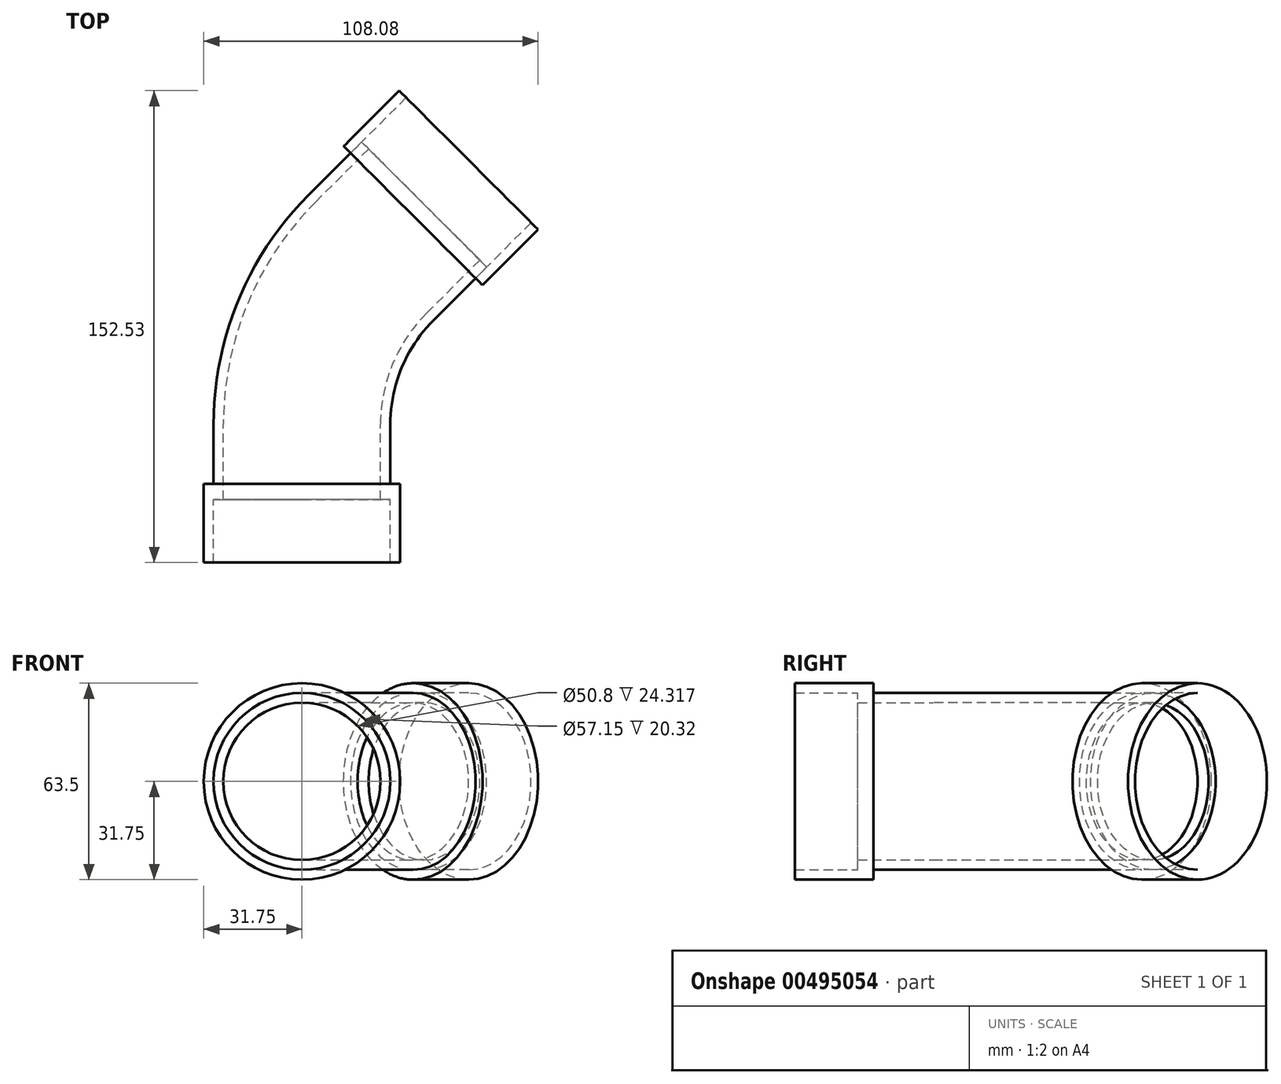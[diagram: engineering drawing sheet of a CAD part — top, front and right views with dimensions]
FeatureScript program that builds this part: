
annotation { "Feature Type Name" : "Feature", "Feature Type Description" : "" }
export const myFeature = defineFeature(function(context is Context, id is Id, definition is map)
    precondition{}
    {
        {
            var Q0;
            Q0=qCreatedBy(makeId("Front.planeOp"),FACE);
            var sketch = newSketch(context, id + "F0", { "sketchPlane" : qUnion([Q0])});
            skCircle(sketch, "E0", {"center": v(0, 0) * mm, "radius": 25.4 * mm});
            skCircle(sketch, "E1", {"center": v(0, 0) * mm, "radius": 28.58 * mm});
            skCircle(sketch, "E2", {"center": v(0, 0) * mm, "radius": 31.75 * mm});
            skSolve(sketch);
        }
        {
            var Q0;
            Q0=qCreatedBy(makeId("Top.planeOp"),FACE);
            var sketch = newSketch(context, id + "F1", { "sketchPlane" : qUnion([Q0])});
            skLineSegment(sketch, "E3", {"start": v(0, 0) * mm, "end": v(0, 19.24) * mm});
            skLineSegment(sketch, "E4.bottom", {"start": v(0, 50.8) * mm, "end": v(35.92, 50.8) * mm});
            skLineSegment(sketch, "E4.top", {"start": v(0, 86.72) * mm, "end": v(35.92, 86.72) * mm});
            skLineSegment(sketch, "E4.left", {"start": v(0, 50.8) * mm, "end": v(0, 86.72) * mm});
            skLineSegment(sketch, "E4.right", {"start": v(35.92, 50.8) * mm, "end": v(35.92, 86.72) * mm});
            skLineSegment(sketch, "E5", {"start": v(22.32, 73.12) * mm, "end": v(35.92, 86.72) * mm});
            skPoint(sketch, "E6.visualSharp", {"position": v(0, 50.8) * mm});
            skArc(sketch, "E6.filletArc", {"start": v(22.32, 73.12) * mm, "mid": v(5.8, 48.4) * mm, "end": v(0, 19.24) * mm});
            skSolve(sketch);
        }
        {
            var Q0;
            Q0=makeQuery(id+"F0.imprint","IMPRINT",FACE,{"disambiguationData":[TD([[makeQuery(id+"F0.imprint","IMPRINT",EDGE,{"derivedFrom":sQuery(id+"F0.wireOp",EDGE,"E0")}),-1.0]])]});
            var Q1;
            Q1=sQuery(id+"F1.wireOp",EDGE,"E3");
            var Q2;
            Q2=sQuery(id+"F1.wireOp",EDGE,"E6.filletArc");
            var Q3;
            Q3=sQuery(id+"F1.wireOp",EDGE,"E5");
            sweep(context, id + "F2", {"profiles" : qUnion([Q0]), "path" : qUnion([Q1, Q2, Q3])});
        }
        {
            var Q0;
            Q0=makeQuery(id+"F0.imprint","IMPRINT",FACE,{"disambiguationData":[TD([[makeQuery(id+"F0.imprint","IMPRINT",EDGE,{"derivedFrom":sQuery(id+"F0.wireOp",EDGE,"E0")}),-1.0]])]});
            extrude(context, id + "F3", {"entities" : qUnion([Q0]), "operationType" : NewBodyOperationType.ADD, "depth" : 5.08 * mm});
        }
        {
            var Q0;
            Q0=makeQuery(id+"F0.imprint","IMPRINT",FACE,{"disambiguationData":[TD([[makeQuery(id+"F0.imprint","IMPRINT",EDGE,{"derivedFrom":sQuery(id+"F0.wireOp",EDGE,"E1")}),-1.0]])]});
            var Q1;
            Q1=sQuery(id+"F0.wireOp",EDGE,"E2");
            extrude(context, id + "F4", {"entities" : qUnion([Q0]), "operationType" : NewBodyOperationType.ADD, "surfaceEntities" : qUnion([Q1]), "depth" : 25.4 * mm});
        }
        {
            var Q0;
            Q0=makeQuery(id+"F2.opSweep","CAP_FACE",FACE,{"disambiguationData":[OSD([sQuery(id+"F0.wireOp",EDGE,"E0"),sQuery(id+"F0.wireOp",EDGE,"E1"),sQuery(id+"F1.wireOp",VERTEX,"E5.end")])],"isStart":false});
            var sketch = newSketch(context, id + "F5", { "sketchPlane" : qUnion([Q0])});
            skCircle(sketch, "E7.0", {"center": v(35.92, 0) * mm, "radius": 25.4 * mm});
            skCircle(sketch, "E8.0", {"center": v(35.92, 0) * mm, "radius": 28.58 * mm});
            skCircle(sketch, "E9", {"center": v(35.92, 0) * mm, "radius": 31.75 * mm});
            skSolve(sketch);
        }
        {
            var Q0;
            Q0=qSketchRegion(id+"F5",true);
            extrude(context, id + "F6", {"entities" : qUnion([Q0]), "depth" : 25.4 * mm});
        }
        {
            var Q0;
            Q0=makeQuery(id+"F2.opSweep","CAP_FACE",FACE,{"disambiguationData":[OSD([sQuery(id+"F0.wireOp",EDGE,"E0"),sQuery(id+"F0.wireOp",EDGE,"E1"),sQuery(id+"F1.wireOp",VERTEX,"E5.end")])],"isStart":false});
            extrude(context, id + "F7", {"entities" : qUnion([Q0]), "depth" : 5.08 * mm});
        }
    });
